FCSTD DOCUMENT
Label: Case_Bottom
objects: Sketcher::SketchObject×1
note: 1 computed .brp shape members not serialized (recipe doc carries the construction recipe); baked Part::Feature solids carry a one-line shape summary decoded from their .brp

FEATURE [Sketcher::SketchObject] Sketch
  sketch-geometry (12):
    g0: LineSegment StartX=-35 StartY=-51 StartZ=0 EndX=-35 EndY=50 EndZ=0
    g1: LineSegment StartX=35 StartY=50 StartZ=0 EndX=35 EndY=-51 EndZ=0
    g2: LineSegment StartX=-30 StartY=55 StartZ=0 EndX=30 EndY=55 EndZ=0
    g3: LineSegment StartX=-30 StartY=-56 StartZ=0 EndX=-13.5 EndY=-56 EndZ=0
    g4: LineSegment StartX=30 StartY=-56 StartZ=0 EndX=16.5 EndY=-56 EndZ=0
    g5: ArcOfCircle CenterX=-30 CenterY=50 CenterZ=0 NormalX=0 NormalY=0 NormalZ=1 Radius=5 StartAngle=1.5708 EndAngle=3.14159
    g6: ArcOfCircle CenterX=30 CenterY=50 CenterZ=0 NormalX=0 NormalY=0 NormalZ=1 Radius=5 StartAngle=0 EndAngle=1.5708
    g7: ArcOfCircle CenterX=30 CenterY=-51 CenterZ=0 NormalX=0 NormalY=0 NormalZ=1 Radius=5 StartAngle=4.71239 EndAngle=6.28319
    g8: ArcOfCircle CenterX=-30 CenterY=-51 CenterZ=0 NormalX=0 NormalY=0 NormalZ=1 Radius=5 StartAngle=3.14159 EndAngle=4.71239
    g9: ArcOfCircle CenterX=-13.5 CenterY=-61 CenterZ=0 NormalX=0 NormalY=0 NormalZ=1 Radius=5 StartAngle=0.643501 EndAngle=1.5708
    g10: ArcOfCircle CenterX=16.5 CenterY=-61 CenterZ=0 NormalX=0 NormalY=0 NormalZ=1 Radius=5 StartAngle=1.5708 EndAngle=2.49809
    g11: LineSegment StartX=-9.5 StartY=-58 StartZ=0 EndX=12.5 EndY=-58 EndZ=0
  constraints (32):
    c: Vertical(g0)
    c: Vertical(g1)
    c: Horizontal(g2)
    c: Horizontal(g3)
    c: Horizontal(g4)
    c: Tangent(g0,g5)
    c: Tangent(g2,g5)
    c: Tangent(g2,g6)
    c: Tangent(g1,g6)
    c: Tangent(g4,g7)
    c: Tangent(g1,g7)
    c: Tangent(g3,g8)
    c: Tangent(g0,g8)
    c: Tangent(g3,g9)
    c: Tangent(g4,g10)
    c: DistanceX(g0,g2) = 5
    c: DistanceX(g2,g1) = 5
    c: DistanceY(g2,g4) = -111
    c: DistanceY(g-1,g2) = 55
    c: Radius(g8) = 5
    c: Radius(g7) = 5
    c: Radius(g10) = 5
    c: Radius(g9) = 5
    c: Coincident(g11,g9)
    c: Coincident(g11,g10)
    c: Horizontal(g11)
    c: DistanceX(g3,g4) = 30
    c: DistanceY(g9,g3) = 2
    c: DistanceX(g10,g1) = 22.5
    c: DistanceX(g0,g1) = 70
    c: DistanceX(g-1,g2) = -30
    c: DistanceY(g2,g3) = -111
